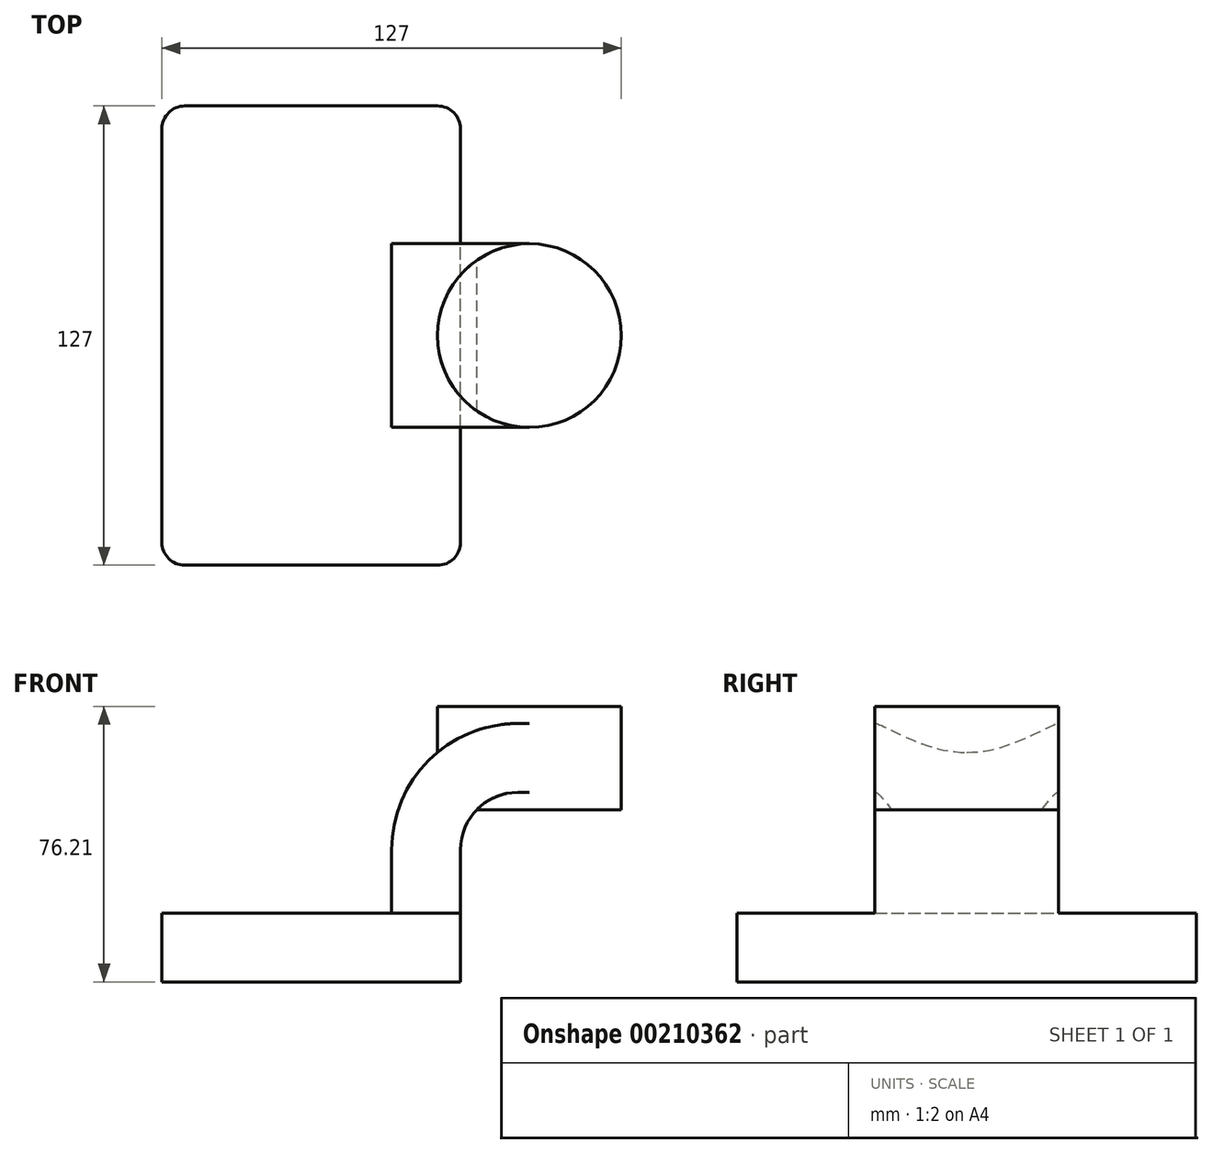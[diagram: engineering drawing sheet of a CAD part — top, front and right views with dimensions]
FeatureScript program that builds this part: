
annotation { "Feature Type Name" : "Feature", "Feature Type Description" : "" }
export const myFeature = defineFeature(function(context is Context, id is Id, definition is map)
    precondition{}
    {
        {
            var Q0;
            Q0=qCreatedBy(makeId("Front.planeOp"),FACE);
            var sketch = newSketch(context, id + "F0", { "sketchPlane" : qUnion([Q0])});
            skLineSegment(sketch, "E0.bottom", {"start": v(41.28, -9.52) * mm, "end": v(-41.28, -9.53) * mm});
            skLineSegment(sketch, "E0.top", {"start": v(41.28, 9.53) * mm, "end": v(-41.28, 9.53) * mm});
            skLineSegment(sketch, "E0.left", {"start": v(41.28, -9.52) * mm, "end": v(41.28, 9.53) * mm});
            skLineSegment(sketch, "E0.right", {"start": v(-41.28, -9.53) * mm, "end": v(-41.28, 9.53) * mm});
            skPoint(sketch, "E0.middle", {"position": v(0, 0) * mm});
            skLineSegment(sketch, "E1.bottom", {"start": v(111.12, 38.1) * mm, "end": v(60.33, 38.1) * mm});
            skLineSegment(sketch, "E1.top", {"start": v(111.13, 66.68) * mm, "end": v(60.33, 66.68) * mm});
            skLineSegment(sketch, "E1.left", {"start": v(111.12, 38.1) * mm, "end": v(111.12, 66.68) * mm});
            skLineSegment(sketch, "E1.right", {"start": v(60.33, 38.1) * mm, "end": v(60.33, 66.68) * mm});
            skPoint(sketch, "E1.middle", {"position": v(85.72, 52.39) * mm});
            skLineSegment(sketch, "E2", {"start": v(41.28, 9.53) * mm, "end": v(41.28, 27) * mm});
            skArc(sketch, "E3", {"start": v(41.27, 27) * mm, "mid": v(45.92, 38.23) * mm, "end": v(57.15, 42.88) * mm});
            skLineSegment(sketch, "E4", {"start": v(57.15, 42.88) * mm, "end": v(85.72, 42.88) * mm});
            skLineSegment(sketch, "E5.0", {"start": v(57.15, 61.93) * mm, "end": v(85.72, 61.93) * mm});
            skArc(sketch, "E5.1", {"start": v(22.23, 27) * mm, "mid": v(32.45, 51.7) * mm, "end": v(57.15, 61.93) * mm});
            skLineSegment(sketch, "E5.2", {"start": v(22.22, 9.53) * mm, "end": v(22.22, 27) * mm});
            skLineSegment(sketch, "E6", {"start": v(85.72, 38.1) * mm, "end": v(85.73, 66.68) * mm});
            skFitSpline(sketch, "E7", {"points": [v(-41.28, 9.52) * mm, v(57.15, 61.93) * mm], "startDerivative": vector(2.12, 88.1) * mm, "endDerivative": vector(175.38, -4.85) * mm});
            skSolve(sketch);
        }
        {
            var Q0;
            Q0=makeQuery(id+"F0.imprint","IMPRINT",FACE,{"disambiguationData":[TD([[makeQuery(id+"F0.imprint","IMPRINT",EDGE,{"derivedFrom":sQuery(id+"F0.wireOp",EDGE,"E0.bottom")}),-1.0]])]});
            extrude(context, id + "F1", {"entities" : qUnion([Q0]), "endBound" : BoundingType.SYMMETRIC, "depth" : 127 * mm});
        }
        {
            var Q0;
            {var subQ1=sQuery(id+"F0.wireOp",EDGE,"E2");Q0=makeQuery(id+"F0.imprint","IMPRINT",FACE,{"disambiguationData":[TD([[makeQuery(id+"F0.imprint","IMPRINT",EDGE,{"derivedFrom":subQ1}),1.0]])]});}
            extrude(context, id + "F2", {"entities" : qUnion([Q0]), "operationType" : NewBodyOperationType.ADD, "endBound" : BoundingType.SYMMETRIC, "depth" : 50.8 * mm});
        }
        {
            var Q0;
            Q0=makeQuery(id+"F0.imprint","IMPRINT",FACE,{"disambiguationData":[TD([[makeQuery(id+"F0.imprint","IMPRINT",EDGE,{"derivedFrom":sQuery(id+"F0.wireOp",EDGE,"E5.1")}),1.0]])]});
            extrude(context, id + "F3", {"entities" : qUnion([Q0]), "operationType" : NewBodyOperationType.ADD, "endBound" : BoundingType.SYMMETRIC, "depth" : 15.88 * mm});
        }
        {
            var Q0;
            {var subQ0=sQuery(id+"F0.wireOp",EDGE,"E1.right");var subQ1=sQuery(id+"F0.wireOp",EDGE,"E1.top");var subQ2=makeQuery(id+"F0.imprint","INTERSECT",VERTEX,{"derivedFrom":[subQ1,subQ0]});Q0=makeQuery(id+"F0.imprint","IMPRINT",FACE,{"disambiguationData":[TD([[makeQuery(id+"F0.imprint","IMPRINT",EDGE,{"disambiguationData":[TD([[subQ2,1.0]])],"derivedFrom":subQ1}),1.0]])]});}
            var Q1;
            {var subQ0=sQuery(id+"F0.wireOp",EDGE,"E4");var subQ1=sQuery(id+"F0.wireOp",EDGE,"E1.right");var subQ2=makeQuery(id+"F0.imprint","INTERSECT",VERTEX,{"derivedFrom":[subQ1,subQ0]});Q1=makeQuery(id+"F0.imprint","IMPRINT",FACE,{"disambiguationData":[TD([[makeQuery(id+"F0.imprint","IMPRINT",EDGE,{"disambiguationData":[TD([[subQ2,-1.0]])],"derivedFrom":subQ1}),-1.0]])]});}
            var Q2;
            {var subQ0=sQuery(id+"F0.wireOp",EDGE,"E1.right");var subQ1=sQuery(id+"F0.wireOp",EDGE,"E1.bottom");var subQ2=makeQuery(id+"F0.imprint","INTERSECT",VERTEX,{"derivedFrom":[subQ1,subQ0]});Q2=makeQuery(id+"F0.imprint","IMPRINT",FACE,{"disambiguationData":[TD([[makeQuery(id+"F0.imprint","IMPRINT",EDGE,{"disambiguationData":[TD([[subQ2,1.0]])],"derivedFrom":subQ1}),-1.0]])]});}
            var Q3;
            Q3=sQuery(id+"F0.wireOp",EDGE,"E1.right");
            revolve(context, id + "F4", {"operationType" : NewBodyOperationType.ADD, "entities" : qUnion([Q0, Q1, Q2]), "axis" : qUnion([Q3]), "revolveType" : RevolveType.FULL});
        }
        {
            var Q0;
            Q0=makeQuery(id+"F1.opExtrude","CAP_EDGE",EDGE,{"disambiguationData":[OSD([sQuery(id+"F0.wireOp",EDGE,"E0.right")])],"isStart":false});
            var Q1;
            Q1=makeQuery(id+"F1.opExtrude","CAP_EDGE",EDGE,{"disambiguationData":[OSD([sQuery(id+"F0.wireOp",EDGE,"E0.left")])],"isStart":false});
            var Q2;
            Q2=makeQuery(id+"F1.opExtrude","CAP_EDGE",EDGE,{"disambiguationData":[OSD([sQuery(id+"F0.wireOp",EDGE,"E0.left")])],"isStart":true});
            var Q3;
            Q3=makeQuery(id+"F1.opExtrude","CAP_EDGE",EDGE,{"disambiguationData":[OSD([sQuery(id+"F0.wireOp",EDGE,"E0.right")])],"isStart":true});
            fillet(context, id + "F5", {"entities" : qUnion([Q0, Q1, Q2, Q3]), "radius" : 6.35 * mm, "tangentPropagation" : true, "allowEdgeOverflow" : false});
        }
    });
